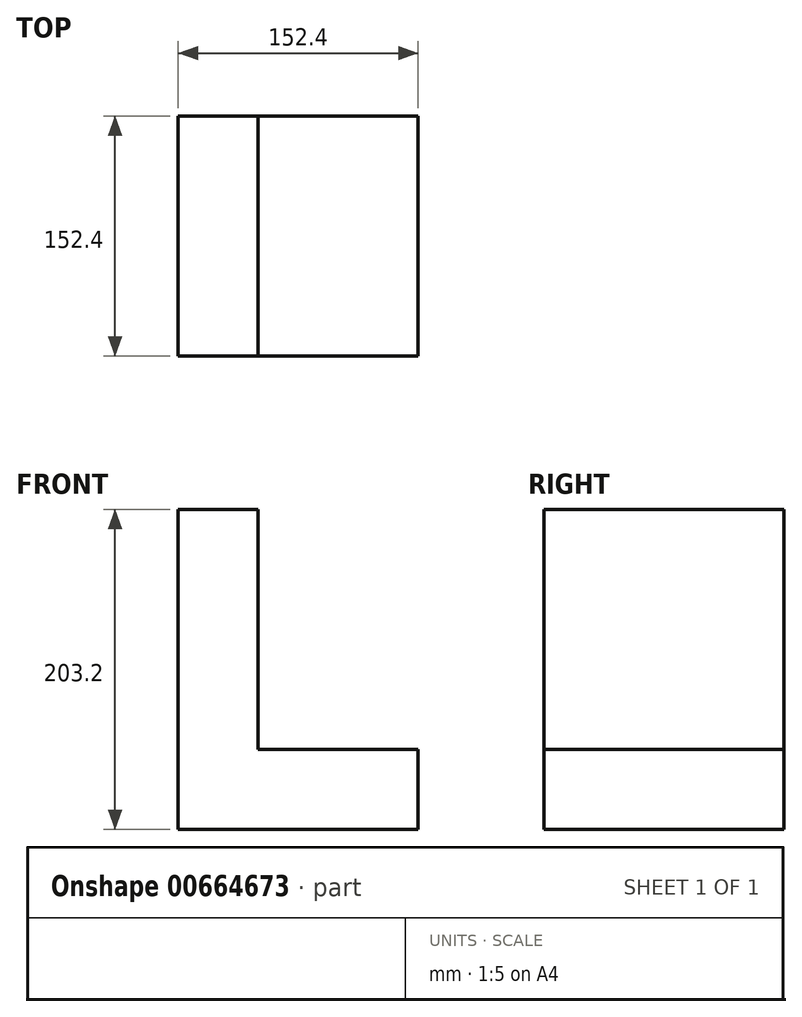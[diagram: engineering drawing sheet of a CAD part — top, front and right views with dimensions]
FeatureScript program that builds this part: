
annotation { "Feature Type Name" : "Feature", "Feature Type Description" : "" }
export const myFeature = defineFeature(function(context is Context, id is Id, definition is map)
    precondition{}
    {
        {
            var Q0;
            Q0=qCreatedBy(makeId("Front.planeOp"),FACE);
            var sketch = newSketch(context, id + "F0", { "sketchPlane" : qUnion([Q0])});
            skLineSegment(sketch, "E0", {"start": v(-50.83, 104.4) * mm, "end": v(-50.83, -98.8) * mm});
            skLineSegment(sketch, "E1", {"start": v(-50.83, -98.8) * mm, "end": v(101.57, -98.8) * mm});
            skLineSegment(sketch, "E2", {"start": v(101.57, -98.8) * mm, "end": v(101.57, -48) * mm});
            skLineSegment(sketch, "E3", {"start": v(-50.83, 104.4) * mm, "end": v(-0.03, 104.4) * mm});
            skLineSegment(sketch, "E4", {"start": v(101.57, -48) * mm, "end": v(0, -48) * mm});
            skLineSegment(sketch, "E5", {"start": v(-0.03, 104.4) * mm, "end": v(0, -48) * mm});
            skSolve(sketch);
        }
        {
            var Q0;
            Q0 = qSketchRegion(id + "F0", true);
            var Q1;
            Q1=makeQuery(id+"F0.imprint","IMPRINT",FACE,{"disambiguationData":[TD([[makeQuery(id+"F0.imprint","IMPRINT",EDGE,{"derivedFrom":sQuery(id+"F0.wireOp",EDGE,"E0")}),1.0]])]});
            extrude(context, id + "F1", {"entities" : qUnion([Q0, Q1]), "depth" : 152.4 * mm, "offsetDistance" : 25.4 * mm});
        }
    });
